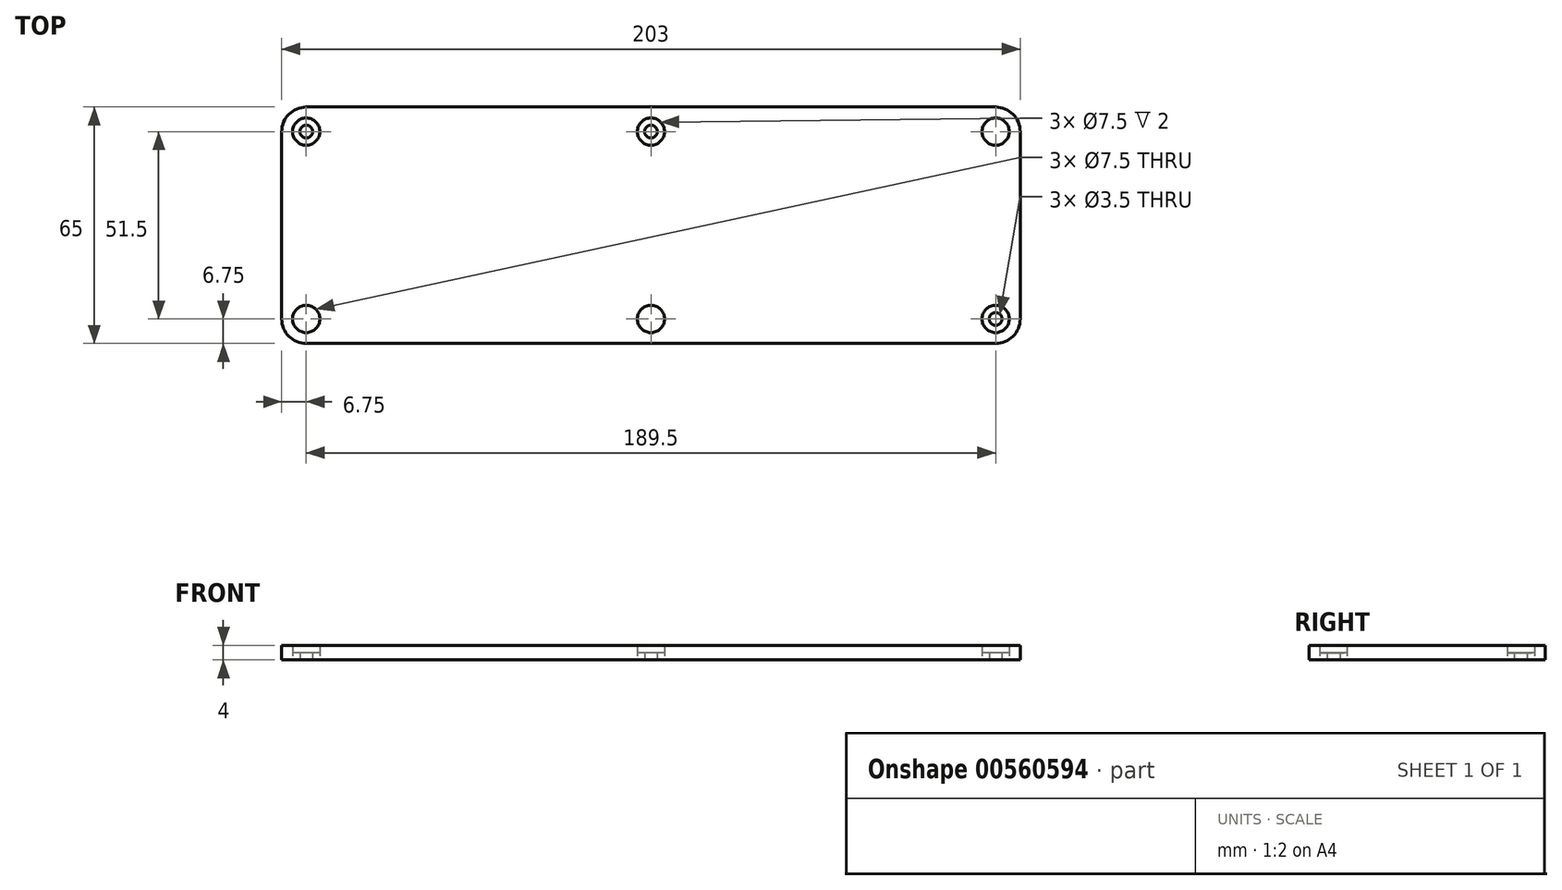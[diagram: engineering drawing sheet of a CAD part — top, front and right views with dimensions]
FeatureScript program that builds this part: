
annotation { "Feature Type Name" : "Feature", "Feature Type Description" : "" }
export const myFeature = defineFeature(function(context is Context, id is Id, definition is map)
    precondition{}
    {
        {
            var Q0;
            Q0=qCreatedBy(makeId("Top.planeOp"),FACE);
            var sketch = newSketch(context, id + "F0", { "sketchPlane" : qUnion([Q0])});
            skLineSegment(sketch, "E0.bottom", {"start": v(94.75, -32.5) * mm, "end": v(-94.75, -32.5) * mm});
            skLineSegment(sketch, "E0.top", {"start": v(94.75, 32.5) * mm, "end": v(-94.75, 32.5) * mm});
            skLineSegment(sketch, "E0.left", {"start": v(101.5, -25.75) * mm, "end": v(101.5, 25.75) * mm});
            skLineSegment(sketch, "E0.right", {"start": v(-101.5, -25.75) * mm, "end": v(-101.5, 25.75) * mm});
            skCircle(sketch, "E1", {"center": v(-94.75, 25.75) * mm, "radius": 3.75 * mm});
            skCircle(sketch, "E2", {"center": v(-94.75, 25.75) * mm, "radius": 1.75 * mm});
            skPoint(sketch, "E3.orphan", {"position": v(-101.5, 32.5) * mm});
            skArc(sketch, "E4.trimOffspring", {"start": v(-94.75, 32.5) * mm, "mid": v(-99.52, 30.52) * mm, "end": v(-101.5, 25.75) * mm});
            skArc(sketch, "E5.MirrorCS", {"start": v(94.75, 32.5) * mm, "mid": v(99.52, 30.52) * mm, "end": v(101.5, 25.75) * mm});
            skCircle(sketch, "E6.MirrorC", {"center": v(94.75, 25.75) * mm, "radius": 3.75 * mm});
            skCircle(sketch, "E7.MirrorC", {"center": v(94.75, 25.75) * mm, "radius": 1.75 * mm});
            skArc(sketch, "E8.MirrorCS", {"start": v(-94.75, -32.5) * mm, "mid": v(-99.52, -30.52) * mm, "end": v(-101.5, -25.75) * mm});
            skCircle(sketch, "E9.MirrorC", {"center": v(-94.75, -25.75) * mm, "radius": 3.75 * mm});
            skCircle(sketch, "E10.MirrorC", {"center": v(-94.75, -25.75) * mm, "radius": 1.75 * mm});
            skArc(sketch, "E11.MirrorCS", {"start": v(94.75, -32.5) * mm, "mid": v(99.52, -30.52) * mm, "end": v(101.5, -25.75) * mm});
            skCircle(sketch, "E12.MirrorC", {"center": v(94.75, -25.75) * mm, "radius": 3.75 * mm});
            skCircle(sketch, "E13.MirrorC", {"center": v(94.75, -25.75) * mm, "radius": 1.75 * mm});
            skPoint(sketch, "E14.orphan", {"position": v(-101.5, -32.5) * mm});
            skPoint(sketch, "E15.orphan", {"position": v(101.5, -32.5) * mm});
            skPoint(sketch, "E16.orphan", {"position": v(101.5, 32.5) * mm});
            skCircle(sketch, "E17", {"center": v(0, 25.75) * mm, "radius": 1.75 * mm});
            skCircle(sketch, "E18", {"center": v(0, 25.75) * mm, "radius": 3.75 * mm});
            skCircle(sketch, "E19.MirrorC", {"center": v(0, -25.75) * mm, "radius": 3.75 * mm});
            skCircle(sketch, "E20.MirrorC", {"center": v(0, -25.75) * mm, "radius": 1.75 * mm});
            skSolve(sketch);
        }
        {
            var Q0;
            Q0=makeQuery(id+"F0.imprint","IMPRINT",FACE,{"disambiguationData":[TD([[makeQuery(id+"F0.imprint","IMPRINT",EDGE,{"derivedFrom":sQuery(id+"F0.wireOp",EDGE,"E0.bottom")}),-1.0]])]});
            extrude(context, id + "F1", {"entities" : qUnion([Q0]), "depth" : 4 * mm, "offsetDistance" : 25 * mm});
        }
        {
            var Q0;
            Q0=makeQuery(id+"F0.imprint","IMPRINT",FACE,{"disambiguationData":[TD([[makeQuery(id+"F0.imprint","IMPRINT",EDGE,{"derivedFrom":sQuery(id+"F0.wireOp",EDGE,"E1")}),1.0]])]});
            var Q1;
            Q1=makeQuery(id+"F0.imprint","IMPRINT",FACE,{"disambiguationData":[TD([[makeQuery(id+"F0.imprint","IMPRINT",EDGE,{"derivedFrom":sQuery(id+"F0.wireOp",EDGE,"E17")}),-1.0]])]});
            var Q2;
            Q2=makeQuery(id+"F0.imprint","IMPRINT",FACE,{"disambiguationData":[TD([[makeQuery(id+"F0.imprint","IMPRINT",EDGE,{"derivedFrom":sQuery(id+"F0.wireOp",EDGE,"E9.MirrorC")}),-1.0]])]});
            var Q3;
            Q3=makeQuery(id+"F0.imprint","IMPRINT",FACE,{"disambiguationData":[TD([[makeQuery(id+"F0.imprint","IMPRINT",EDGE,{"derivedFrom":sQuery(id+"F0.wireOp",EDGE,"E19.MirrorC")}),-1.0]])]});
            var Q4;
            Q4=makeQuery(id+"F0.imprint","IMPRINT",FACE,{"disambiguationData":[TD([[makeQuery(id+"F0.imprint","IMPRINT",EDGE,{"derivedFrom":sQuery(id+"F0.wireOp",EDGE,"E12.MirrorC")}),1.0]])]});
            var Q5;
            Q5=makeQuery(id+"F0.imprint","IMPRINT",FACE,{"disambiguationData":[TD([[makeQuery(id+"F0.imprint","IMPRINT",EDGE,{"derivedFrom":sQuery(id+"F0.wireOp",EDGE,"E6.MirrorC")}),-1.0]])]});
            extrude(context, id + "F2", {"entities" : qUnion([Q0, Q1, Q2, Q3, Q4, Q5]), "operationType" : NewBodyOperationType.ADD, "depth" : 2 * mm, "offsetDistance" : 25 * mm});
        }
    });
